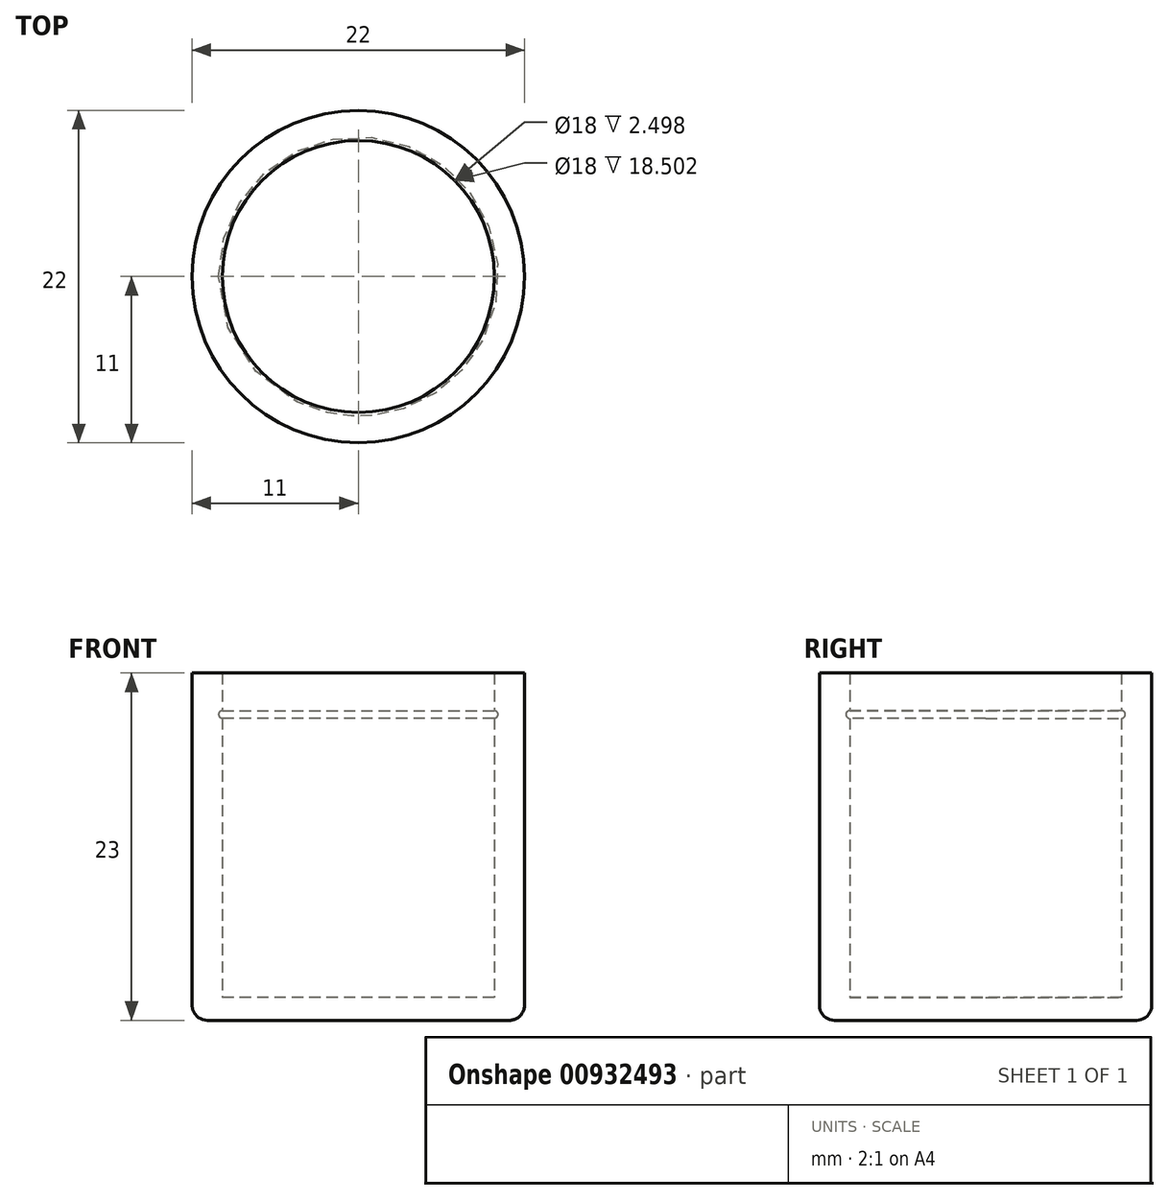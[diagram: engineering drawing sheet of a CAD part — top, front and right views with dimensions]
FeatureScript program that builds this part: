
annotation { "Feature Type Name" : "Feature", "Feature Type Description" : "" }
export const myFeature = defineFeature(function(context is Context, id is Id, definition is map)
    precondition{}
    {
        {
            var Q0;
            Q0=qCreatedBy(makeId("Top.planeOp"),FACE);
            var sketch = newSketch(context, id + "F0", { "sketchPlane" : qUnion([Q0])});
            skPoint(sketch, "E0.middle", {"position": v(0, 0) * mm});
            skPoint(sketch, "E1.orphan", {"position": v(0, 42.68) * mm});
            skPoint(sketch, "E0.bottom.start.orphan", {"position": v(42.68, 42.68) * mm});
            skPoint(sketch, "E0.top.start.orphan", {"position": v(42.68, -42.68) * mm});
            skPoint(sketch, "E0.right.end.orphan", {"position": v(-42.68, -42.68) * mm});
            skPoint(sketch, "E0.right.start.orphan", {"position": v(-42.68, 42.68) * mm});
            skCircle(sketch, "E2", {"center": v(0, 0) * mm, "radius": 9 * mm});
            skSolve(sketch);
        }
        {
            var Q0;
            Q0=makeQuery(id+"F0.imprint","IMPRINT",FACE,{"disambiguationData":[TD([[makeQuery(id+"F0.imprint","IMPRINT",EDGE,{"derivedFrom":sQuery(id+"F0.wireOp",EDGE,"E2")}),1.0]])]});
            extrude(context, id + "F1", {"entities" : qUnion([Q0]), "depth" : 1.5 * mm, "offsetDistance" : 25 * mm});
        }
        {
            var Q0;
            Q0=qCreatedBy(makeId("Top.planeOp"),FACE);
            var sketch = newSketch(context, id + "F2", { "sketchPlane" : qUnion([Q0])});
            skCircle(sketch, "E3", {"center": v(0, 0) * mm, "radius": 11 * mm});
            skCircle(sketch, "E4", {"center": v(0, 0) * mm, "radius": 9 * mm});
            skSolve(sketch);
        }
        {
            var Q0;
            Q0=makeQuery(id+"F2.imprint","IMPRINT",FACE,{"disambiguationData":[TD([[makeQuery(id+"F2.imprint","IMPRINT",EDGE,{"derivedFrom":sQuery(id+"F2.wireOp",EDGE,"E3")}),1.0]])]});
            extrude(context, id + "F3", {"entities" : qUnion([Q0]), "operationType" : NewBodyOperationType.ADD, "depth" : 23 * mm, "offsetDistance" : 25 * mm});
        }
        {
            var Q0;
            Q0=qCreatedBy(makeId("Front.planeOp"),FACE);
            var sketch = newSketch(context, id + "F4", { "sketchPlane" : qUnion([Q0])});
            skLineSegment(sketch, "E5", {"start": v(9, 22.75) * mm, "end": v(9, 20.25) * mm});
            skCircle(sketch, "E6", {"center": v(9, 20.25) * mm, "radius": 0.25 * mm});
            skLineSegment(sketch, "E7", {"start": v(0, 0) * mm, "end": v(0, 32.02) * mm});
            skSolve(sketch);
        }
        {
            var Q0;
            Q0 = qSketchRegion(id + "F4", true);
            var Q1;
            Q1=makeQuery(id+"F3.opExtrude","SWEPT_FACE",FACE,{"disambiguationData":[OSD([sQuery(id+"F2.wireOp",EDGE,"E3")])]});
            revolve(context, id + "F5", {"operationType" : NewBodyOperationType.REMOVE, "surfaceOperationType" : NewSurfaceOperationType.NEW, "entities" : qUnion([Q0]), "axis" : qUnion([Q1]), "revolveType" : RevolveType.FULL, "oppositeDirection" : true});
        }
        {
            var Q0;
            Q0=makeQuery(id+"F1.opExtrude","CAP_EDGE",EDGE,{"disambiguationData":[OSD([sQuery(id+"F0.wireOp",EDGE,"E2")])],"isStart":false});
            var Q1;
            Q1=makeQuery(id+"F3.opExtrude","CAP_EDGE",EDGE,{"disambiguationData":[OSD([sQuery(id+"F2.wireOp",EDGE,"E3")])],"isStart":true});
            fillet(context, id + "F6", {"entities" : qUnion([Q0, Q1]), "tangentPropagation" : true, "radius" : 1 * mm, "defaultsChanged" : false, "vertexSettings" : [], "allowEdgeOverflow" : false});
        }
    });
